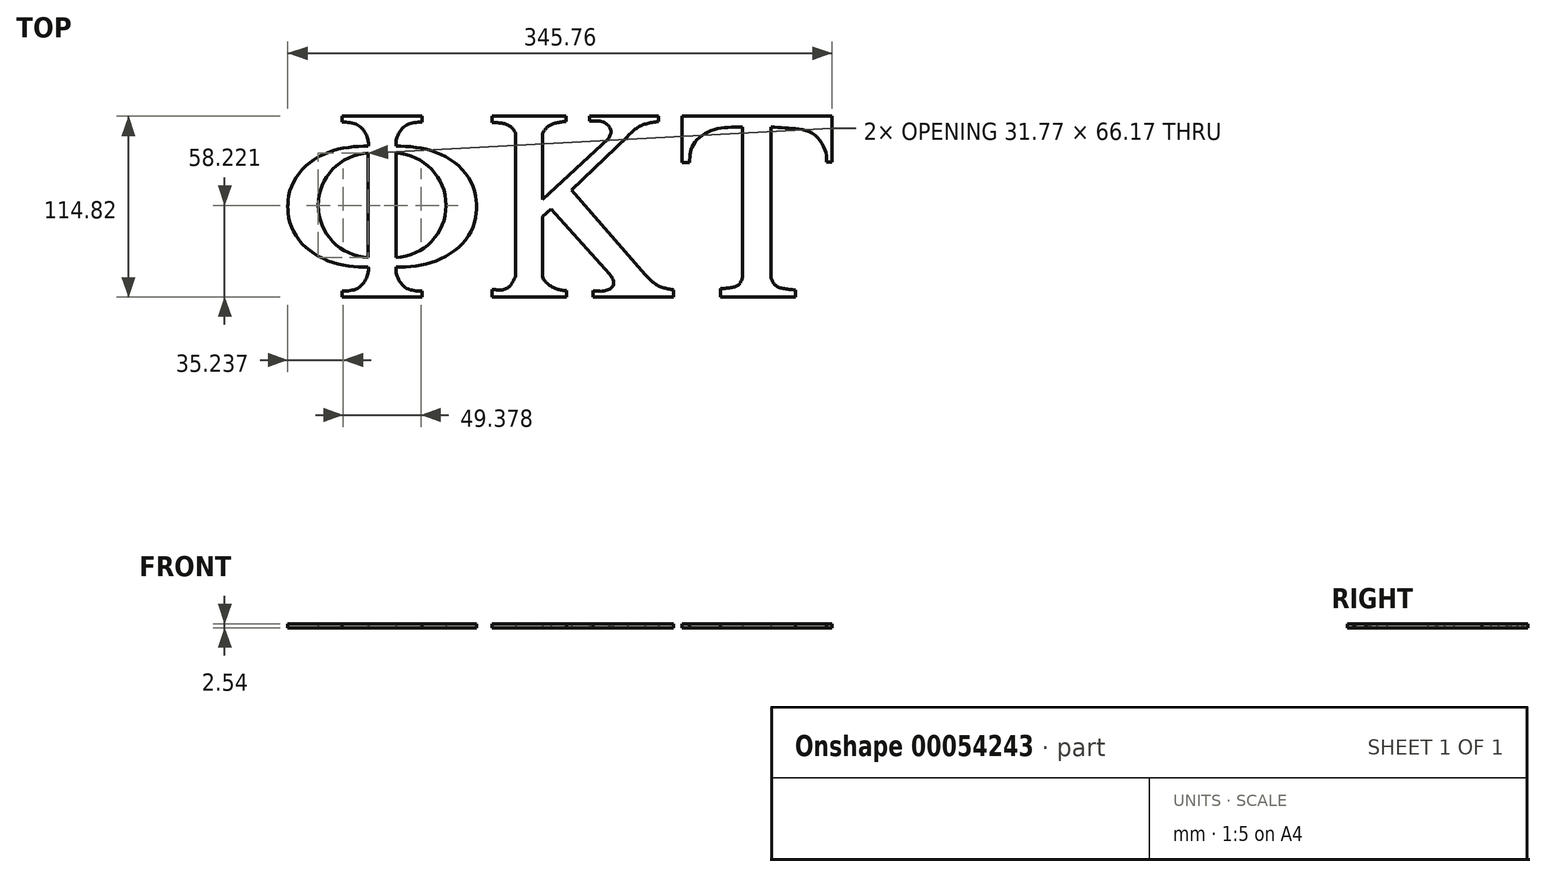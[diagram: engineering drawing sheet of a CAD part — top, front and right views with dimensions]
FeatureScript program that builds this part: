
annotation { "Feature Type Name" : "Feature", "Feature Type Description" : "" }
export const myFeature = defineFeature(function(context is Context, id is Id, definition is map)
    precondition{}
    {
        {
            var Q0;
            Q0=qCreatedBy(makeId("Top.planeOp"),FACE);
            var sketch = newSketch(context, id + "F0", { "sketchPlane" : qUnion([Q0])});
            skLineSegment(sketch, "E0", {"start": v(-95.16, 57.4) * mm, "end": v(-44.36, 57.4) * mm});
            skLineSegment(sketch, "E1", {"start": v(-44.36, 57.4) * mm, "end": v(-44.36, 53.72) * mm});
            skLineSegment(sketch, "E2", {"start": v(-95.16, 57.4) * mm, "end": v(-95.16, 53.57) * mm});
            skLineSegment(sketch, "E3", {"start": v(-60.96, 33.9) * mm, "end": v(-60.96, 0) * mm});
            skArc(sketch, "E4", {"start": v(-60.96, -32.27) * mm, "mid": v(-29.2, 0.81) * mm, "end": v(-60.96, 33.9) * mm});
            skFitSpline(sketch, "E5", {"points": [v(-60.96, 38.52) * mm, v(-41.81, 36.4) * mm, v(-23.5, 27.72) * mm, v(-11.92, 12.36) * mm, v(-9.85, 0) * mm], "startDerivative": vector(68.59, -1) * mm, "endDerivative": vector(-1.31, -32.96) * mm});
            skFitSpline(sketch, "E6.MirrorCS", {"points": [v(-60.96, -38.52) * mm, v(-41.81, -36.4) * mm, v(-23.5, -27.72) * mm, v(-11.92, -12.36) * mm, v(-9.85, 0) * mm], "startDerivative": vector(68.59, 1) * mm, "endDerivative": vector(-1.31, 32.96) * mm});
            skLineSegment(sketch, "E7.MirrorCS", {"start": v(-60.96, -33.9) * mm, "end": v(-60.96, 0) * mm});
            skLineSegment(sketch, "E8", {"start": v(-69.76, 57.4) * mm, "end": v(-69.76, -57.4) * mm});
            skLineSegment(sketch, "E9.MirrorCS", {"start": v(-78.57, 33.9) * mm, "end": v(-78.57, 0) * mm});
            skArc(sketch, "E10.MirrorCS", {"start": v(-78.57, -32.27) * mm, "mid": v(-110.34, 0.81) * mm, "end": v(-78.57, 33.9) * mm});
            skLineSegment(sketch, "E11.MirrorCS", {"start": v(-78.57, -33.9) * mm, "end": v(-78.57, 0) * mm});
            skFitSpline(sketch, "E12.MirrorCS", {"points": [v(-78.57, 38.52) * mm, v(-97.72, 36.4) * mm, v(-116.03, 27.72) * mm, v(-127.6, 12.36) * mm, v(-129.68, 0) * mm], "startDerivative": vector(-68.59, -1) * mm, "endDerivative": vector(1.31, -32.96) * mm});
            skFitSpline(sketch, "E13.MirrorCS", {"points": [v(-78.57, -38.52) * mm, v(-97.72, -36.4) * mm, v(-116.03, -27.72) * mm, v(-127.6, -12.36) * mm, v(-129.68, 0) * mm], "startDerivative": vector(-68.59, 1) * mm, "endDerivative": vector(1.31, 32.96) * mm});
            skFitSpline(sketch, "E14", {"points": [v(-44.36, 53.72) * mm, v(-55.05, 51.35) * mm, v(-60.68, 42.78) * mm, v(-60.96, 38.52) * mm], "startDerivative": vector(-30.02, -1.07) * mm, "endDerivative": vector(1.13, -15.68) * mm});
            skFitSpline(sketch, "E15.MirrorCS", {"points": [v(-95.16, 53.72) * mm, v(-84.47, 51.35) * mm, v(-78.85, 42.78) * mm, v(-78.57, 38.52) * mm], "startDerivative": vector(30.02, -1.07) * mm, "endDerivative": vector(-1.13, -15.68) * mm});
            skFitSpline(sketch, "E16.MirrorCS", {"points": [v(-44.36, -53.72) * mm, v(-55.05, -51.35) * mm, v(-60.68, -42.78) * mm, v(-60.96, -38.52) * mm], "startDerivative": vector(-30.02, 1.07) * mm, "endDerivative": vector(1.13, 15.68) * mm});
            skFitSpline(sketch, "E17.MirrorCS", {"points": [v(-95.16, -53.72) * mm, v(-84.47, -51.35) * mm, v(-78.85, -42.78) * mm, v(-78.57, -38.52) * mm], "startDerivative": vector(30.02, 1.07) * mm, "endDerivative": vector(-1.13, 15.68) * mm});
            skLineSegment(sketch, "E18.MirrorCS", {"start": v(-95.16, -57.4) * mm, "end": v(-44.36, -57.4) * mm});
            skLineSegment(sketch, "E19.MirrorCS", {"start": v(-44.36, -57.4) * mm, "end": v(-44.36, -53.72) * mm});
            skLineSegment(sketch, "E20.MirrorCS", {"start": v(-95.16, -57.4) * mm, "end": v(-95.16, -53.57) * mm});
            skLineSegment(sketch, "E21", {"start": v(15.03, -44.26) * mm, "end": v(15.03, 46.66) * mm});
            skLineSegment(sketch, "E22", {"start": v(32.08, 46.47) * mm, "end": v(32.08, 4.42) * mm});
            skLineSegment(sketch, "E23", {"start": v(32.08, 4.42) * mm, "end": v(73.94, 43.25) * mm});
            skLineSegment(sketch, "E24", {"start": v(32.08, -6.18) * mm, "end": v(37.57, -1.5) * mm});
            skLineSegment(sketch, "E25", {"start": v(37.57, -1.5) * mm, "end": v(74.69, -42.76) * mm});
            skLineSegment(sketch, "E26", {"start": v(32.08, -6.18) * mm, "end": v(32.08, -43.72) * mm});
            skLineSegment(sketch, "E27", {"start": v(86.17, 44.65) * mm, "end": v(50.69, 10.37) * mm});
            skLineSegment(sketch, "E28", {"start": v(50.69, 10.37) * mm, "end": v(97.3, -43.15) * mm});
            skLineSegment(sketch, "E29", {"start": v(0, 57.4) * mm, "end": v(46.96, 57.4) * mm});
            skLineSegment(sketch, "E30", {"start": v(0, -57.4) * mm, "end": v(47.46, -57.4) * mm});
            skLineSegment(sketch, "E31", {"start": v(47.46, -57.4) * mm, "end": v(47.46, -53.44) * mm});
            skLineSegment(sketch, "E32", {"start": v(0, -57.4) * mm, "end": v(0, -52.53) * mm});
            skLineSegment(sketch, "E33", {"start": v(64.27, -57.4) * mm, "end": v(64.27, -53.35) * mm});
            skLineSegment(sketch, "E34", {"start": v(115.44, -57.4) * mm, "end": v(115.44, -52.95) * mm});
            skFitSpline(sketch, "E35", {"points": [v(115.44, -52.95) * mm, v(105.4, -50.14) * mm, v(97.3, -43.15) * mm], "startDerivative": vector(-21.22, 3.61) * mm, "endDerivative": vector(-15.08, 15.96) * mm});
            skFitSpline(sketch, "E36", {"points": [v(64.27, -53.35) * mm, v(72.3, -53.35) * mm, v(77.24, -49.27) * mm, v(74.69, -42.76) * mm], "startDerivative": vector(23.08, -3.15) * mm, "endDerivative": vector(-13.6, 20.75) * mm});
            skFitSpline(sketch, "E37", {"points": [v(0, -52.53) * mm, v(8.02, -52.53) * mm, v(15.03, -44.26) * mm], "startDerivative": vector(6.76, 0) * mm, "endDerivative": vector(10.47, 21.7) * mm});
            skFitSpline(sketch, "E38", {"points": [v(47.46, -53.44) * mm, v(38.89, -51.4) * mm, v(32.08, -43.72) * mm], "startDerivative": vector(-18.97, 1.68) * mm, "endDerivative": vector(-2.1, 19.77) * mm});
            skFitSpline(sketch, "E39", {"points": [v(32.08, 46.47) * mm, v(36.58, 51.67) * mm, v(46.96, 54.08) * mm], "startDerivative": vector(8.18, 13.3) * mm, "endDerivative": vector(21.1, 2.3) * mm});
            skFitSpline(sketch, "E40", {"points": [v(15.03, 46.66) * mm, v(10.57, 51.67) * mm, v(0, 53.48) * mm], "startDerivative": vector(-8.15, 13.14) * mm, "endDerivative": vector(-21.4, 0.96) * mm});
            skLineSegment(sketch, "E41", {"start": v(0, 53.48) * mm, "end": v(0, 57.4) * mm});
            skLineSegment(sketch, "E42", {"start": v(46.96, 54.08) * mm, "end": v(46.96, 57.4) * mm});
            skFitSpline(sketch, "E43", {"points": [v(73.94, 43.25) * mm, v(75.52, 47.77) * mm, v(71.76, 53.18) * mm, v(61.84, 54.38) * mm], "startDerivative": vector(9.22, 15.5) * mm, "endDerivative": vector(-27.36, -1.03) * mm});
            skLineSegment(sketch, "E44", {"start": v(61.84, 54.38) * mm, "end": v(61.84, 57.4) * mm});
            skLineSegment(sketch, "E45", {"start": v(105.89, 57.4) * mm, "end": v(105.89, 54.08) * mm});
            skFitSpline(sketch, "E46", {"points": [v(86.17, 44.65) * mm, v(94.16, 51.22) * mm, v(105.89, 54.08) * mm], "startDerivative": vector(15.2, 15.64) * mm, "endDerivative": vector(24.13, 3.38) * mm});
            skLineSegment(sketch, "E47", {"start": v(159, 50.54) * mm, "end": v(159, -45.1) * mm});
            skLineSegment(sketch, "E48", {"start": v(177.22, 50.56) * mm, "end": v(177.22, -45.44) * mm});
            skFitSpline(sketch, "E49", {"points": [v(159, -45.1) * mm, v(156.3, -49.91) * mm, v(145.21, -52.06) * mm], "startDerivative": vector(-4.02, -13.36) * mm, "endDerivative": vector(-22.45, -1.27) * mm});
            skFitSpline(sketch, "E50", {"points": [v(159, 50.54) * mm, v(139.85, 48.42) * mm, v(127.51, 38.76) * mm, v(125.55, 28.04) * mm], "startDerivative": vector(-52.64, 0.03) * mm, "endDerivative": vector(-0.63, -38.82) * mm});
            skLineSegment(sketch, "E51", {"start": v(125.55, 28.04) * mm, "end": v(120.54, 28.04) * mm});
            skLineSegment(sketch, "E52", {"start": v(120.54, 28.04) * mm, "end": v(120.54, 57.4) * mm});
            skLineSegment(sketch, "E53", {"start": v(216.07, 57.4) * mm, "end": v(216.07, 28.22) * mm});
            skLineSegment(sketch, "E54", {"start": v(216.07, 28.22) * mm, "end": v(212.44, 28.22) * mm});
            skLineSegment(sketch, "E55", {"start": v(145.21, -52.06) * mm, "end": v(145.21, -57.4) * mm});
            skFitSpline(sketch, "E56", {"points": [v(177.22, -45.44) * mm, v(180.61, -50.45) * mm, v(192.77, -52.95) * mm], "startDerivative": vector(5.72, -13.8) * mm, "endDerivative": vector(24.3, -1.92) * mm});
            skLineSegment(sketch, "E57", {"start": v(192.77, -52.95) * mm, "end": v(192.77, -57.4) * mm});
            skFitSpline(sketch, "E58", {"points": [v(177.22, 50.56) * mm, v(191.04, 49.62) * mm, v(204, 46.22) * mm, v(211.87, 34.74) * mm, v(212.44, 28.22) * mm], "startDerivative": vector(50.54, -3.26) * mm, "endDerivative": vector(-1.55, -31.64) * mm});
            skLineSegment(sketch, "E59.trimOffspring", {"start": v(64.27, -57.4) * mm, "end": v(115.44, -57.4) * mm});
            skLineSegment(sketch, "E60.trimOffspring", {"start": v(145.21, -57.4) * mm, "end": v(192.77, -57.4) * mm});
            skLineSegment(sketch, "E61.trimOffspring", {"start": v(120.54, 57.4) * mm, "end": v(216.07, 57.4) * mm});
            skLineSegment(sketch, "E62.trimOffspring", {"start": v(61.84, 57.4) * mm, "end": v(105.89, 57.4) * mm});
            skSolve(sketch);
        }
        {
            var Q0;
            {var subQ8=sQuery(id+"F0.wireOp",EDGE,"E8");Q0=makeQuery(id+"F0.imprint","IMPRINT",FACE,{"disambiguationData":[TD([[makeQuery(id+"F0.imprint","IMPRINT",EDGE,{"derivedFrom":subQ8}),-1.0]])]});}
            var Q1;
            {var subQ6=sQuery(id+"F0.wireOp",EDGE,"E1");Q1=makeQuery(id+"F0.imprint","IMPRINT",FACE,{"disambiguationData":[TD([[makeQuery(id+"F0.imprint","IMPRINT",EDGE,{"derivedFrom":subQ6}),-1.0]])]});}
            var Q2;
            Q2=makeQuery(id+"F0.imprint","IMPRINT",FACE,{"disambiguationData":[TD([[makeQuery(id+"F0.imprint","IMPRINT",EDGE,{"derivedFrom":sQuery(id+"F0.wireOp",EDGE,"E21")}),-1.0]])]});
            var Q3;
            Q3=makeQuery(id+"F0.imprint","IMPRINT",FACE,{"disambiguationData":[TD([[makeQuery(id+"F0.imprint","IMPRINT",EDGE,{"derivedFrom":sQuery(id+"F0.wireOp",EDGE,"E47")}),1.0]])]});
            extrude(context, id + "F1", {"entities" : qUnion([Q0, Q1, Q2, Q3]), "depth" : 2.54 * mm});
        }
        {
            var Q0;
            Q0=makeQuery(id+"F1.opExtrude","CAP_FACE",FACE,{"disambiguationData":[OSD([sQuery(id+"F0.wireOp",EDGE,"E0"),sQuery(id+"F0.wireOp",EDGE,"E1"),sQuery(id+"F0.wireOp",EDGE,"E2"),sQuery(id+"F0.wireOp",EDGE,"E3"),sQuery(id+"F0.wireOp",EDGE,"E4"),sQuery(id+"F0.wireOp",EDGE,"E5"),sQuery(id+"F0.wireOp",EDGE,"E6.MirrorCS"),sQuery(id+"F0.wireOp",EDGE,"E7.MirrorCS"),sQuery(id+"F0.wireOp",EDGE,"E9.MirrorCS"),sQuery(id+"F0.wireOp",EDGE,"E10.MirrorCS"),sQuery(id+"F0.wireOp",EDGE,"E11.MirrorCS"),sQuery(id+"F0.wireOp",EDGE,"E12.MirrorCS"),sQuery(id+"F0.wireOp",EDGE,"E13.MirrorCS"),sQuery(id+"F0.wireOp",EDGE,"E14"),sQuery(id+"F0.wireOp",EDGE,"E15.MirrorCS"),sQuery(id+"F0.wireOp",EDGE,"E16.MirrorCS"),sQuery(id+"F0.wireOp",EDGE,"E17.MirrorCS"),sQuery(id+"F0.wireOp",EDGE,"E18.MirrorCS"),sQuery(id+"F0.wireOp",EDGE,"E19.MirrorCS"),sQuery(id+"F0.wireOp",EDGE,"E20.MirrorCS")])],"isStart":true});
            var sketch = newSketch(context, id + "F2", { "sketchPlane" : qUnion([Q0])});
            skLineSegment(sketch, "E63.bottom", {"start": v(-229, 114.31) * mm, "end": v(373.57, 114.31) * mm});
            skLineSegment(sketch, "E63.top", {"start": v(-229, -129.28) * mm, "end": v(373.57, -129.28) * mm});
            skLineSegment(sketch, "E63.left", {"start": v(-229, 114.31) * mm, "end": v(-229, -129.28) * mm});
            skLineSegment(sketch, "E63.right", {"start": v(373.57, 114.31) * mm, "end": v(373.57, -129.28) * mm});
            skSolve(sketch);
        }
        {
            var Q0;
            Q0 = qSketchRegion(id + "F2", true);
            extrude(context, id + "F3", {"entities" : qUnion([Q0]), "depth" : 2.54 * mm});
        }
        {
            var Q0;
            Q0=makeQuery(id+"F3.opExtrude","SWEPT_BODY",BODY,{"disambiguationData":[OSD([sQuery(id+"F2.wireOp",EDGE,"E63.bottom"),sQuery(id+"F2.wireOp",EDGE,"E63.top"),sQuery(id+"F2.wireOp",EDGE,"E63.left"),sQuery(id+"F2.wireOp",EDGE,"E63.right")])]});
            deleteBodies(context, id + "F4", {"entities" : qUnion([Q0])});
        }
    });
